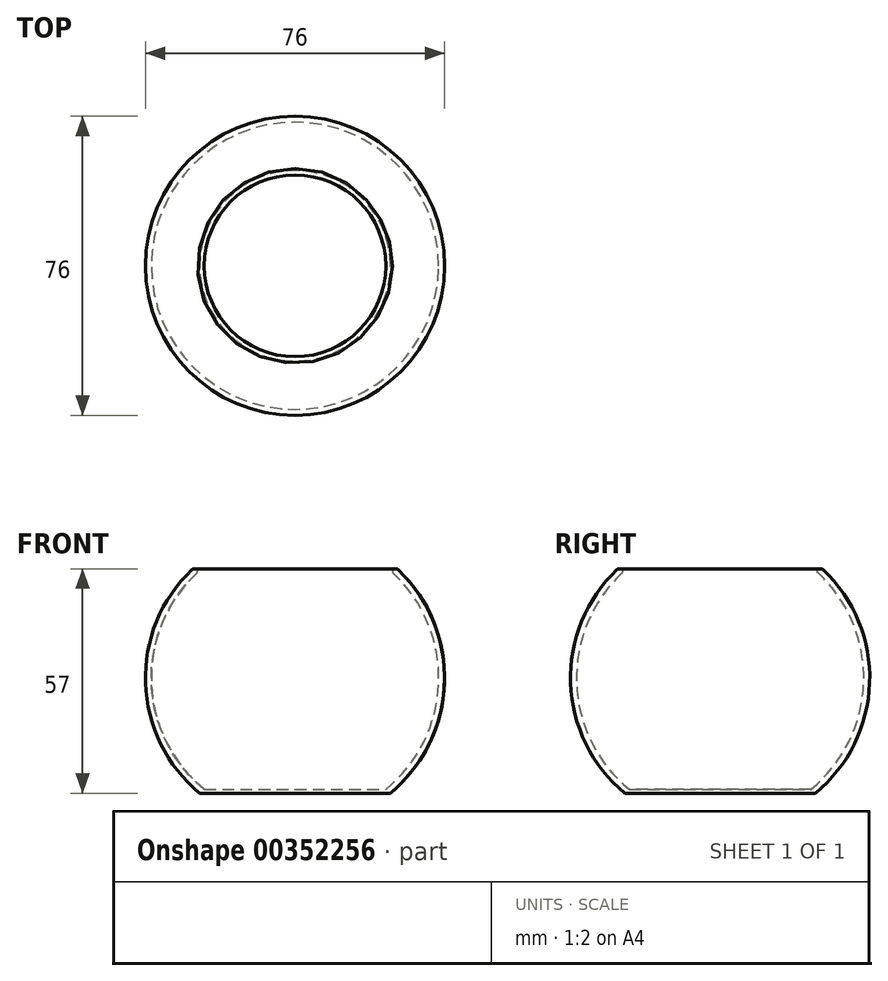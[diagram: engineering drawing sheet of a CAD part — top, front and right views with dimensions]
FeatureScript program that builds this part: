
annotation { "Feature Type Name" : "Feature", "Feature Type Description" : "" }
export const myFeature = defineFeature(function(context is Context, id is Id, definition is map)
    precondition{}
    {
        {
            var Q0;
            Q0=qCreatedBy(makeId("Front.planeOp"),FACE);
            var sketch = newSketch(context, id + "F0", { "sketchPlane" : qUnion([Q0])});
            skCircle(sketch, "E0", {"center": v(0, 0) * mm, "radius": 38 * mm});
            skLineSegment(sketch, "E1", {"start": v(-26, 27.72) * mm, "end": v(26, 27.72) * mm});
            skLineSegment(sketch, "E2", {"start": v(-24.22, -29.28) * mm, "end": v(24.22, -29.28) * mm});
            skCircle(sketch, "E3", {"center": v(0, 0) * mm, "radius": 36.5 * mm});
            skLineSegment(sketch, "E4", {"start": v(0, 83.34) * mm, "end": v(0, -91.2) * mm, "construction": true});
            skPoint(sketch, "E5", {"position": v(-23.75, 27.72) * mm});
            skPoint(sketch, "E6", {"position": v(23.75, 27.72) * mm});
            skSolve(sketch);
        }
        {
            var Q0;
            {var subQ0=sQuery(id+"F0.wireOp",EDGE,"E1");var subQ1=sQuery(id+"F0.wireOp",EDGE,"E0");var subQ2=makeQuery(id+"F0.imprint","INTERSECT",VERTEX,{"disambiguationData":[OD(1.0)],"derivedFrom":[subQ1,subQ0]});Q0=makeQuery(id+"F0.imprint","IMPRINT",FACE,{"disambiguationData":[TD([[makeQuery(id+"F0.imprint","IMPRINT",EDGE,{"disambiguationData":[TD([[subQ2,1.0]])],"derivedFrom":subQ1}),1.0]])]});}
            var Q1;
            Q1=sQuery(id+"F0.wireOp",EDGE,"E4");
            revolve(context, id + "F1", {"surfaceOperationType" : NewSurfaceOperationType.NEW, "entities" : qUnion([Q0]), "axis" : qUnion([Q1]), "revolveType" : RevolveType.FULL});
        }
        {
            var Q0;
            Q0=makeQuery(id+"F1.opRevolve","SWEPT_FACE",FACE,{"disambiguationData":[OSD([sQuery(id+"F0.wireOp",EDGE,"E2")])]});
            var sketch = newSketch(context, id + "F2", { "sketchPlane" : qUnion([Q0])});
            skCircle(sketch, "E7", {"center": v(0, 0) * mm, "radius": 21.5 * mm});
            skSolve(sketch);
        }
        {
            var Q0;
            Q0=makeQuery(id+"F2.imprint","IMPRINT",FACE,{"disambiguationData":[TD([[makeQuery(id+"F2.imprint","IMPRINT",EDGE,{"derivedFrom":makeQuery(id+"F1.opRevolve","SWEPT_EDGE",EDGE,{"disambiguationData":[OSD([sQuery(id+"F0.wireOp",EDGE,"E2"),sQuery(id+"F0.wireOp",EDGE,"E3")])]})}),-1.0]])]});
            var Q1;
            {var subQ0=sQuery(id+"F0.wireOp",EDGE,"E2");Q1=makeQuery(id+"F2.imprint","IMPRINT",FACE,{"disambiguationData":[TD([[makeQuery(id+"F2.imprint","IMPRINT",EDGE,{"derivedFrom":makeQuery(id+"F1.opRevolve","SWEPT_EDGE",EDGE,{"disambiguationData":[OSD([sQuery(id+"F0.wireOp",EDGE,"E0"),subQ0])]})}),-1.0]])]});}
            var Q2;
            Q2=makeQuery(id+"F2.imprint","IMPRINT",FACE,{"disambiguationData":[TD([[makeQuery(id+"F2.imprint","IMPRINT",EDGE,{"derivedFrom":sQuery(id+"F2.wireOp",EDGE,"E7")}),1.0]])]});
            extrude(context, id + "F3", {"entities" : qUnion([Q0, Q1, Q2]), "operationType" : NewBodyOperationType.ADD, "oppositeDirection" : true, "depth" : 1 * mm, "offsetDistance" : 25 * mm});
        }
        {
            var Q0;
            Q0=makeQuery(id+"F1.opRevolve","SWEPT_EDGE",EDGE,{"disambiguationData":[OSD([sQuery(id+"F0.wireOp",EDGE,"E0"),sQuery(id+"F0.wireOp",EDGE,"E1")])]});
            var Q1;
            Q1=makeQuery(id+"F1.opRevolve","SWEPT_EDGE",EDGE,{"disambiguationData":[OSD([sQuery(id+"F0.wireOp",EDGE,"E1"),sQuery(id+"F0.wireOp",EDGE,"E3")])]});
            fillet(context, id + "F4", {"entities" : qUnion([Q0, Q1]), "radius" : .6 * mm, "tangentPropagation" : true, "defaultsChanged" : true, "vertexSettings" : [], "allowEdgeOverflow" : false});
        }
    });
